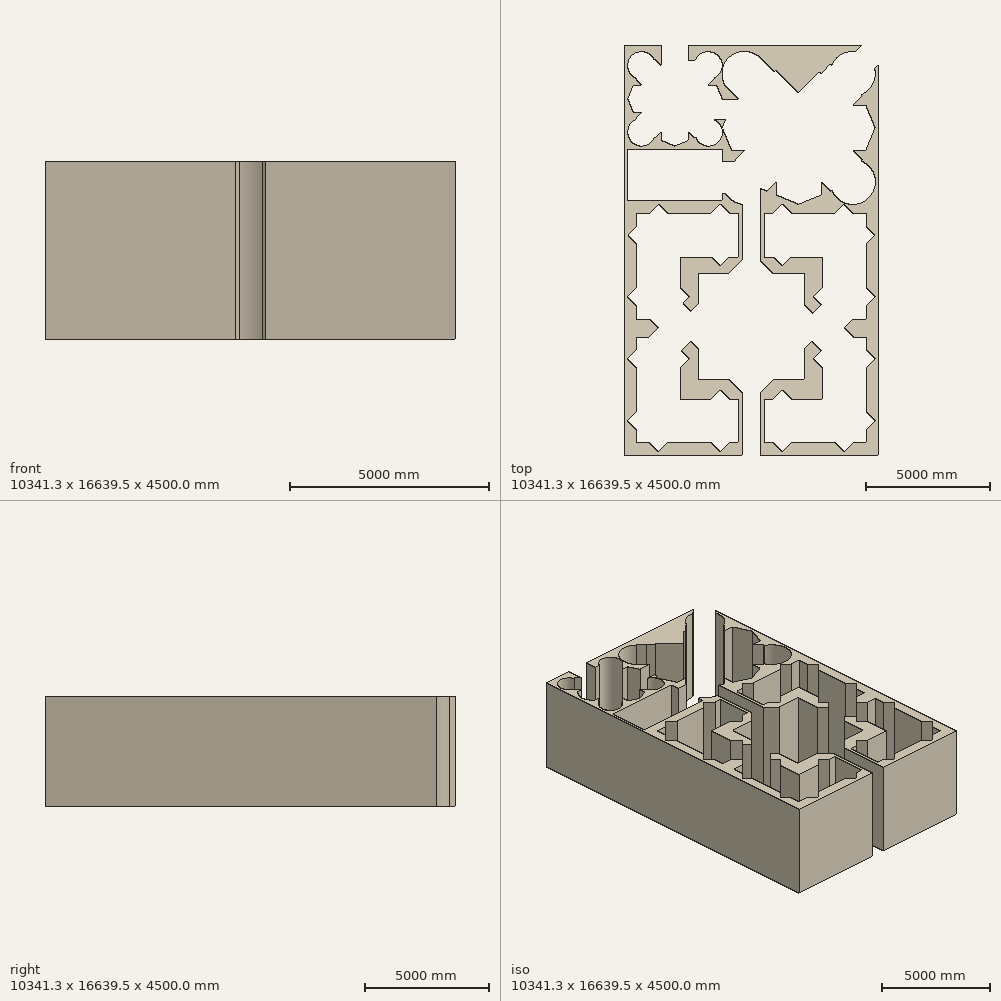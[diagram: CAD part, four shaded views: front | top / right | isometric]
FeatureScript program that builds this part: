
annotation { "Feature Type Name" : "Feature", "Feature Type Description" : "" }
export const myFeature = defineFeature(function(context is Context, id is Id, definition is map)
    precondition{}
    {
        {
            var Q0;
            Q0=qCreatedBy(makeId("Top.planeOp"),FACE);
            var sketch = newSketch(context, id + "F0", { "sketchPlane" : qUnion([Q0])});
            skLineSegment(sketch, "E0", {"start": v(6052.83, 6645.12) * mm, "end": v(5685.2, 6277.49) * mm});
            skLineSegment(sketch, "E1", {"start": v(6052.83, 5389.96) * mm, "end": v(6572.74, 5389.96) * mm});
            skLineSegment(sketch, "E2", {"start": v(6052.83, 9155.44) * mm, "end": v(5685.2, 8787.81) * mm});
            skLineSegment(sketch, "E3", {"start": v(6052.83, 10410.6) * mm, "end": v(6572.74, 10410.6) * mm});
            skLineSegment(sketch, "E4", {"start": v(5685.2, 13808.46) * mm, "end": v(6052.83, 13440.84) * mm});
            skLineSegment(sketch, "E5", {"start": v(6052.83, 14176.1) * mm, "end": v(5685.2, 13808.46) * mm});
            skLineSegment(sketch, "E6", {"start": v(8563.16, 12920.93) * mm, "end": v(9083.06, 12920.93) * mm});
            skLineSegment(sketch, "E7", {"start": v(9818.32, 12920.93) * mm, "end": v(10188.23, 12920.93) * mm});
            skLineSegment(sketch, "E8", {"start": v(10188.23, 12920.93) * mm, "end": v(10188.23, 14696) * mm});
            skLineSegment(sketch, "E9", {"start": v(10188.23, 14696) * mm, "end": v(9818.32, 14696) * mm});
            skLineSegment(sketch, "E10", {"start": v(9818.32, 5389.96) * mm, "end": v(10188.23, 5389.96) * mm});
            skLineSegment(sketch, "E11", {"start": v(10188.23, 7165.02) * mm, "end": v(9818.32, 7165.02) * mm});
            skLineSegment(sketch, "E12", {"start": v(11223.48, 5389.96) * mm, "end": v(11593.39, 5389.96) * mm});
            skLineSegment(sketch, "E13", {"start": v(13583.8, 7165.02) * mm, "end": v(12328.65, 7165.02) * mm});
            skLineSegment(sketch, "E14", {"start": v(11593.39, 7165.02) * mm, "end": v(11223.48, 7165.02) * mm});
            skLineSegment(sketch, "E15", {"start": v(13540.37, 9112) * mm, "end": v(13216.18, 8787.81) * mm});
            skLineSegment(sketch, "E16", {"start": v(13216.18, 11298.14) * mm, "end": v(13540.37, 10973.95) * mm});
            skLineSegment(sketch, "E17", {"start": v(13583.8, 11665.77) * mm, "end": v(13216.18, 11298.14) * mm});
            skLineSegment(sketch, "E18", {"start": v(13583.8, 12920.93) * mm, "end": v(13583.8, 11665.77) * mm});
            skLineSegment(sketch, "E19", {"start": v(11223.48, 12920.93) * mm, "end": v(11593.39, 12920.93) * mm});
            skLineSegment(sketch, "E20", {"start": v(12328.65, 12920.93) * mm, "end": v(13583.8, 12920.93) * mm});
            skLineSegment(sketch, "E21", {"start": v(10055.24, 16875.43) * mm, "end": v(10077.3, 16821.95) * mm});
            skLineSegment(sketch, "E22", {"start": v(13609.52, 20438.13) * mm, "end": v(13903.7, 20733.02) * mm});
            skLineSegment(sketch, "E23", {"start": v(6015.44, 18546.52) * mm, "end": v(6032.8, 18504.43) * mm});
            skLineSegment(sketch, "E24", {"start": v(7827.9, 11665.77) * mm, "end": v(7827.9, 12920.93) * mm});
            skLineSegment(sketch, "E25", {"start": v(10188.23, 5389.96) * mm, "end": v(10188.23, 7165.02) * mm});
            skLineSegment(sketch, "E26", {"start": v(8563.16, 12920.93) * mm, "end": v(7827.9, 12920.93) * mm});
            skLineSegment(sketch, "E27", {"start": v(8257.01, 9497.68) * mm, "end": v(8543.44, 9211.25) * mm});
            skLineSegment(sketch, "E28", {"start": v(13148.68, 9503.7) * mm, "end": v(13540.37, 9112) * mm});
            skLineSegment(sketch, "E29", {"start": v(13816.94, 10036.96) * mm, "end": v(14141.14, 9712.77) * mm});
            skLineSegment(sketch, "E30", {"start": v(13210.16, 10643.74) * mm, "end": v(13540.37, 10973.95) * mm});
            skLineSegment(sketch, "E31", {"start": v(13528.56, 20356.5) * mm, "end": v(13903.7, 20733.02) * mm});
            skLineSegment(sketch, "E32", {"start": v(10077.3, 16821.95) * mm, "end": v(9520.98, 16821.95) * mm});
            skLineSegment(sketch, "E33", {"start": v(9654.14, 15488.62) * mm, "end": v(9520.98, 15488.62) * mm});
            skLineSegment(sketch, "E34", {"start": v(9520.98, 15204.7) * mm, "end": v(5685.2, 15204.7) * mm});
            skLineSegment(sketch, "E35", {"start": v(14917.97, 21263) * mm, "end": v(15200.59, 21511.85) * mm});
            skLineSegment(sketch, "E36", {"start": v(9176.96, 18507.2) * mm, "end": v(9520.98, 18507.2) * mm});
            skArc(sketch, "E37", {"start": v(15166.58, 19511.46) * mm, "mid": v(15633.58, 19946.01) * mm, "end": v(15702.28, 20580.2) * mm});
            skArc(sketch, "E38", {"start": v(13978.32, 15621.76) * mm, "mid": v(15468.53, 15323.83) * mm, "end": v(15170.85, 16814.1) * mm});
            skArc(sketch, "E39", {"start": v(6032.8, 18504.43) * mm, "mid": v(5851.1, 17589.86) * mm, "end": v(6764.95, 17775.2) * mm});
            skArc(sketch, "E40", {"start": v(8451.28, 17776.09) * mm, "mid": v(9367.75, 17592.12) * mm, "end": v(9176.96, 18507.2) * mm});
            skArc(sketch, "E41", {"start": v(6762.28, 20910.78) * mm, "mid": v(5847.8, 21093.33) * mm, "end": v(6032.5, 20179.29) * mm});
            skLineSegment(sketch, "E42", {"start": v(9806.63, 12260.86) * mm, "end": v(10338.23, 12792.45) * mm});
            skLineSegment(sketch, "E43", {"start": v(11073.48, 12780.42) * mm, "end": v(11593.05, 12260.86) * mm});
            skLineSegment(sketch, "E44", {"start": v(7038.77, 21511.85) * mm, "end": v(8162.46, 21511.85) * mm});
            skLineSegment(sketch, "E45", {"start": v(10338.23, 4872.33) * mm, "end": v(11073.48, 4872.33) * mm});
            skLineSegment(sketch, "E46", {"start": v(15170.85, 16814.1) * mm, "end": v(15194.5, 16873.27) * mm});
            skLineSegment(sketch, "E47", {"start": v(5685.2, 6277.49) * mm, "end": v(6052.83, 5909.86) * mm});
            skLineSegment(sketch, "E48", {"start": v(6052.83, 5909.86) * mm, "end": v(6052.83, 5389.96) * mm});
            skLineSegment(sketch, "E49", {"start": v(7264.56, 9718.79) * mm, "end": v(6940.37, 10042.98) * mm});
            skLineSegment(sketch, "E50", {"start": v(6940.37, 10042.98) * mm, "end": v(6572.74, 9675.35) * mm});
            skLineSegment(sketch, "E51", {"start": v(6572.74, 9675.35) * mm, "end": v(6052.83, 9675.35) * mm});
            skLineSegment(sketch, "E52", {"start": v(6052.83, 9675.35) * mm, "end": v(6052.83, 9155.44) * mm});
            skLineSegment(sketch, "E53", {"start": v(5685.2, 8787.81) * mm, "end": v(6052.83, 8420.19) * mm});
            skLineSegment(sketch, "E54", {"start": v(6052.83, 8420.19) * mm, "end": v(6052.83, 7900.28) * mm});
            skLineSegment(sketch, "E55", {"start": v(6052.83, 7900.28) * mm, "end": v(6052.83, 6645.12) * mm});
            skLineSegment(sketch, "E56", {"start": v(6572.74, 14696) * mm, "end": v(6052.83, 14696) * mm});
            skLineSegment(sketch, "E57", {"start": v(6052.83, 14696) * mm, "end": v(6052.83, 14176.1) * mm});
            skLineSegment(sketch, "E58", {"start": v(9083.06, 12920.93) * mm, "end": v(9450.7, 12553.3) * mm});
            skLineSegment(sketch, "E59", {"start": v(9450.7, 12553.3) * mm, "end": v(9818.32, 12920.93) * mm});
            skLineSegment(sketch, "E60", {"start": v(9818.32, 14696) * mm, "end": v(9450.7, 15063.63) * mm});
            skLineSegment(sketch, "E61", {"start": v(9450.7, 15063.63) * mm, "end": v(9083.06, 14696) * mm});
            skLineSegment(sketch, "E62", {"start": v(9083.06, 14696) * mm, "end": v(7308, 14696) * mm});
            skLineSegment(sketch, "E63", {"start": v(7308, 14696) * mm, "end": v(6940.37, 15063.63) * mm});
            skLineSegment(sketch, "E64", {"start": v(6940.37, 15063.63) * mm, "end": v(6572.74, 14696) * mm});
            skLineSegment(sketch, "E65", {"start": v(9083.06, 5389.96) * mm, "end": v(9450.7, 5022.33) * mm});
            skLineSegment(sketch, "E66", {"start": v(9450.7, 5022.33) * mm, "end": v(9818.32, 5389.96) * mm});
            skLineSegment(sketch, "E67", {"start": v(9818.32, 7165.02) * mm, "end": v(9450.7, 7532.65) * mm});
            skLineSegment(sketch, "E68", {"start": v(9450.7, 7532.65) * mm, "end": v(9083.06, 7165.02) * mm});
            skLineSegment(sketch, "E69", {"start": v(6572.74, 5389.96) * mm, "end": v(6940.37, 5022.33) * mm});
            skLineSegment(sketch, "E70", {"start": v(6940.37, 5022.33) * mm, "end": v(7308, 5389.96) * mm});
            skLineSegment(sketch, "E71", {"start": v(7308, 5389.96) * mm, "end": v(9083.06, 5389.96) * mm});
            skLineSegment(sketch, "E72", {"start": v(9083.06, 7165.02) * mm, "end": v(7827.9, 7165.02) * mm});
            skLineSegment(sketch, "E73", {"start": v(7827.9, 7165.02) * mm, "end": v(7827.9, 7900.28) * mm});
            skLineSegment(sketch, "E74", {"start": v(7827.9, 7900.28) * mm, "end": v(7827.9, 8420.19) * mm});
            skLineSegment(sketch, "E75", {"start": v(7827.9, 8420.19) * mm, "end": v(8195.53, 8787.81) * mm});
            skLineSegment(sketch, "E76", {"start": v(8195.53, 8787.81) * mm, "end": v(7871.34, 9112) * mm});
            skLineSegment(sketch, "E77", {"start": v(11593.39, 5389.96) * mm, "end": v(11961.02, 5022.33) * mm});
            skLineSegment(sketch, "E78", {"start": v(11961.02, 5022.33) * mm, "end": v(12328.65, 5389.96) * mm});
            skLineSegment(sketch, "E79", {"start": v(12328.65, 7165.02) * mm, "end": v(11961.02, 7532.65) * mm});
            skLineSegment(sketch, "E80", {"start": v(11961.02, 7532.65) * mm, "end": v(11593.39, 7165.02) * mm});
            skLineSegment(sketch, "E81", {"start": v(14103.71, 5389.96) * mm, "end": v(14471.34, 5022.33) * mm});
            skLineSegment(sketch, "E82", {"start": v(14471.34, 5022.33) * mm, "end": v(14838.97, 5389.96) * mm});
            skLineSegment(sketch, "E83", {"start": v(12328.65, 5389.96) * mm, "end": v(13583.8, 5389.96) * mm});
            skLineSegment(sketch, "E84", {"start": v(13583.8, 5389.96) * mm, "end": v(14103.71, 5389.96) * mm});
            skLineSegment(sketch, "E85", {"start": v(14838.97, 5389.96) * mm, "end": v(15358.88, 5389.96) * mm});
            skLineSegment(sketch, "E86", {"start": v(15358.88, 5389.96) * mm, "end": v(15358.88, 5909.86) * mm});
            skLineSegment(sketch, "E87", {"start": v(15358.88, 5909.86) * mm, "end": v(15726.5, 6277.49) * mm});
            skLineSegment(sketch, "E88", {"start": v(15726.5, 6277.49) * mm, "end": v(15358.88, 6645.12) * mm});
            skLineSegment(sketch, "E89", {"start": v(15358.88, 8420.19) * mm, "end": v(15726.5, 8787.81) * mm});
            skLineSegment(sketch, "E90", {"start": v(15726.5, 8787.81) * mm, "end": v(15358.88, 9155.44) * mm});
            skLineSegment(sketch, "E91", {"start": v(14838.97, 9675.35) * mm, "end": v(14471.34, 10042.98) * mm});
            skLineSegment(sketch, "E92", {"start": v(14471.34, 10042.98) * mm, "end": v(14141.14, 9712.77) * mm});
            skLineSegment(sketch, "E93", {"start": v(15358.88, 6645.12) * mm, "end": v(15358.88, 7900.28) * mm});
            skLineSegment(sketch, "E94", {"start": v(15358.88, 7900.28) * mm, "end": v(15358.88, 8420.19) * mm});
            skLineSegment(sketch, "E95", {"start": v(15358.88, 9155.44) * mm, "end": v(15358.88, 9675.35) * mm});
            skLineSegment(sketch, "E96", {"start": v(15358.88, 9675.35) * mm, "end": v(14838.97, 9675.35) * mm});
            skLineSegment(sketch, "E97", {"start": v(13216.18, 8787.81) * mm, "end": v(13583.8, 8420.19) * mm});
            skLineSegment(sketch, "E98", {"start": v(13583.8, 8420.19) * mm, "end": v(13583.8, 7165.02) * mm});
            skLineSegment(sketch, "E99", {"start": v(14838.97, 10410.6) * mm, "end": v(15358.88, 10410.6) * mm});
            skLineSegment(sketch, "E100", {"start": v(15358.88, 10410.6) * mm, "end": v(15358.88, 10930.51) * mm});
            skLineSegment(sketch, "E101", {"start": v(15358.88, 10930.51) * mm, "end": v(15726.5, 11298.14) * mm});
            skLineSegment(sketch, "E102", {"start": v(15726.5, 11298.14) * mm, "end": v(15358.88, 11665.77) * mm});
            skLineSegment(sketch, "E103", {"start": v(14838.97, 14696) * mm, "end": v(14471.34, 15063.63) * mm});
            skLineSegment(sketch, "E104", {"start": v(14471.34, 15063.63) * mm, "end": v(14103.71, 14696) * mm});
            skLineSegment(sketch, "E105", {"start": v(15358.88, 11665.77) * mm, "end": v(15358.88, 12920.93) * mm});
            skLineSegment(sketch, "E106", {"start": v(15358.88, 12920.93) * mm, "end": v(15358.88, 13440.84) * mm});
            skLineSegment(sketch, "E107", {"start": v(15358.88, 13440.84) * mm, "end": v(15726.5, 13808.46) * mm});
            skLineSegment(sketch, "E108", {"start": v(15726.5, 13808.46) * mm, "end": v(15358.88, 14176.1) * mm});
            skLineSegment(sketch, "E109", {"start": v(15358.88, 14176.1) * mm, "end": v(15358.88, 14696) * mm});
            skLineSegment(sketch, "E110", {"start": v(15358.88, 14696) * mm, "end": v(14838.97, 14696) * mm});
            skLineSegment(sketch, "E111", {"start": v(11593.39, 12920.93) * mm, "end": v(11961.02, 12553.3) * mm});
            skLineSegment(sketch, "E112", {"start": v(11961.02, 12553.3) * mm, "end": v(12328.65, 12920.93) * mm});
            skLineSegment(sketch, "E113", {"start": v(12328.65, 14696) * mm, "end": v(11961.02, 15063.63) * mm});
            skLineSegment(sketch, "E114", {"start": v(11961.02, 15063.63) * mm, "end": v(11593.39, 14696) * mm});
            skLineSegment(sketch, "E115", {"start": v(14103.71, 14696) * mm, "end": v(13583.8, 14696) * mm});
            skLineSegment(sketch, "E116", {"start": v(13583.8, 14696) * mm, "end": v(12328.65, 14696) * mm});
            skLineSegment(sketch, "E117", {"start": v(11593.39, 14696) * mm, "end": v(11223.48, 14696) * mm});
            skLineSegment(sketch, "E118", {"start": v(11223.48, 14696) * mm, "end": v(11223.48, 12920.93) * mm});
            skLineSegment(sketch, "E119", {"start": v(10055.24, 16875.43) * mm, "end": v(10433.14, 17254.22) * mm});
            skLineSegment(sketch, "E120", {"start": v(10433.14, 17254.22) * mm, "end": v(9898.48, 17254.22) * mm});
            skLineSegment(sketch, "E121", {"start": v(9898.48, 17254.22) * mm, "end": v(9520.97, 18166.39) * mm});
            skLineSegment(sketch, "E122", {"start": v(15352.05, 17254.22) * mm, "end": v(14819.13, 17254.22) * mm});
            skLineSegment(sketch, "E123", {"start": v(14819.13, 17254.22) * mm, "end": v(15194.5, 16873.27) * mm});
            skLineSegment(sketch, "E124", {"start": v(6572.74, 10410.6) * mm, "end": v(6940.37, 10042.98) * mm});
            skLineSegment(sketch, "E125", {"start": v(6940.37, 10042.98) * mm, "end": v(7264.9, 10367.52) * mm});
            skLineSegment(sketch, "E126", {"start": v(12856.24, 10997.67) * mm, "end": v(12856.24, 12260.86) * mm});
            skLineSegment(sketch, "E127", {"start": v(12856.24, 12260.86) * mm, "end": v(11593.05, 12260.86) * mm});
            skLineSegment(sketch, "E128", {"start": v(9806.63, 7948.06) * mm, "end": v(8543.44, 7948.06) * mm});
            skLineSegment(sketch, "E129", {"start": v(8543.44, 7948.06) * mm, "end": v(8543.44, 9211.25) * mm});
            skLineSegment(sketch, "E130", {"start": v(7589.1, 10043.32) * mm, "end": v(7264.56, 9718.79) * mm});
            skLineSegment(sketch, "E131", {"start": v(7264.56, 9718.79) * mm, "end": v(7589.1, 10043.32) * mm});
            skLineSegment(sketch, "E132", {"start": v(7589.1, 10043.32) * mm, "end": v(7264.9, 10367.52) * mm});
            skLineSegment(sketch, "E133", {"start": v(13816.94, 10036.96) * mm, "end": v(14147.15, 10367.17) * mm});
            skLineSegment(sketch, "E134", {"start": v(14147.15, 10367.17) * mm, "end": v(14471.34, 10042.98) * mm});
            skLineSegment(sketch, "E135", {"start": v(14471.34, 10042.98) * mm, "end": v(14838.97, 10410.6) * mm});
            skLineSegment(sketch, "E136", {"start": v(12623.74, 15063.63) * mm, "end": v(13530.42, 15437.21) * mm});
            skLineSegment(sketch, "E137", {"start": v(13530.42, 15437.21) * mm, "end": v(13530.25, 15979.46) * mm});
            skLineSegment(sketch, "E138", {"start": v(13530.25, 15979.46) * mm, "end": v(13914.31, 15595.4) * mm});
            skLineSegment(sketch, "E139", {"start": v(13914.31, 15595.4) * mm, "end": v(13978.32, 15621.76) * mm});
            skLineSegment(sketch, "E140", {"start": v(14814.35, 17254.22) * mm, "end": v(15349, 17254.22) * mm});
            skLineSegment(sketch, "E141", {"start": v(15349, 17254.22) * mm, "end": v(15726.51, 18166.39) * mm});
            skLineSegment(sketch, "E142", {"start": v(15726.51, 18166.39) * mm, "end": v(15347.51, 19076.56) * mm});
            skLineSegment(sketch, "E143", {"start": v(15347.51, 19076.56) * mm, "end": v(14814.34, 19076.56) * mm});
            skLineSegment(sketch, "E144", {"start": v(9520.98, 18507.2) * mm, "end": v(9662.89, 18507.2) * mm});
            skLineSegment(sketch, "E145", {"start": v(9662.89, 18507.2) * mm, "end": v(9520.97, 18166.39) * mm});
            skLineSegment(sketch, "E146", {"start": v(9173.17, 20180.05) * mm, "end": v(9190.44, 20138.35) * mm});
            skLineSegment(sketch, "E147", {"start": v(9190.44, 20138.35) * mm, "end": v(8954.2, 19901.55) * mm});
            skLineSegment(sketch, "E148", {"start": v(8954.2, 19901.55) * mm, "end": v(9286.23, 19907.1) * mm});
            skLineSegment(sketch, "E149", {"start": v(9286.23, 19907.1) * mm, "end": v(9520.98, 19340.31) * mm});
            skLineSegment(sketch, "E150", {"start": v(9520.98, 19340.31) * mm, "end": v(10169.4, 19340.31) * mm});
            skLineSegment(sketch, "E151", {"start": v(10169.4, 19340.31) * mm, "end": v(9676.55, 19833.16) * mm});
            skLineSegment(sketch, "E152", {"start": v(11073.48, 12780.42) * mm, "end": v(11073.48, 15054.7) * mm});
            skLineSegment(sketch, "E153", {"start": v(11073.48, 15054.7) * mm, "end": v(11073.48, 15333.96) * mm});
            skLineSegment(sketch, "E154", {"start": v(11073.48, 15333.96) * mm, "end": v(11073.48, 15706.8) * mm});
            skLineSegment(sketch, "E155", {"start": v(11073.48, 15706.8) * mm, "end": v(11268.91, 15627.11) * mm});
            skLineSegment(sketch, "E156", {"start": v(11268.91, 15627.11) * mm, "end": v(11345.9, 15595.72) * mm});
            skLineSegment(sketch, "E157", {"start": v(11345.9, 15595.72) * mm, "end": v(11718.06, 15968.75) * mm});
            skLineSegment(sketch, "E158", {"start": v(11718.06, 15968.75) * mm, "end": v(11718.06, 15440.75) * mm});
            skLineSegment(sketch, "E159", {"start": v(11718.06, 15440.75) * mm, "end": v(12623.74, 15063.63) * mm});
            skLineSegment(sketch, "E160", {"start": v(15166.58, 19511.46) * mm, "end": v(15191.76, 19450.69) * mm});
            skLineSegment(sketch, "E161", {"start": v(15191.76, 19450.69) * mm, "end": v(14818.51, 19076.56) * mm});
            skLineSegment(sketch, "E162", {"start": v(14818.51, 19076.56) * mm, "end": v(15346.72, 19076.56) * mm});
            skLineSegment(sketch, "E163", {"start": v(13903.7, 20733.02) * mm, "end": v(13973.1, 20704.32) * mm});
            skArc(sketch, "E164", {"start": v(14917.97, 21263) * mm, "mid": v(14352.24, 21141.45) * mm, "end": v(13973.1, 20704.32) * mm});
            skLineSegment(sketch, "E165", {"start": v(11337.15, 20730.62) * mm, "end": v(11633.78, 20433.98) * mm});
            skLineSegment(sketch, "E166", {"start": v(11633.78, 20433.98) * mm, "end": v(11704.5, 20504.7) * mm});
            skLineSegment(sketch, "E167", {"start": v(11704.5, 20504.7) * mm, "end": v(12621.46, 19587.73) * mm});
            skLineSegment(sketch, "E168", {"start": v(12621.46, 19587.73) * mm, "end": v(13457.72, 20427.08) * mm});
            skLineSegment(sketch, "E169", {"start": v(13457.72, 20427.08) * mm, "end": v(13528.56, 20356.5) * mm});
            skLineSegment(sketch, "E170", {"start": v(9520.98, 16821.95) * mm, "end": v(9520.98, 17276.6) * mm});
            skLineSegment(sketch, "E171", {"start": v(9520.98, 17276.6) * mm, "end": v(5685.2, 17276.6) * mm});
            skLineSegment(sketch, "E172", {"start": v(5685.2, 17276.6) * mm, "end": v(5685.2, 15204.7) * mm});
            skLineSegment(sketch, "E173", {"start": v(5685.2, 15204.7) * mm, "end": v(9520.98, 15204.7) * mm});
            skLineSegment(sketch, "E174", {"start": v(9520.98, 15204.7) * mm, "end": v(9520.98, 15488.62) * mm});
            skLineSegment(sketch, "E175", {"start": v(9520.98, 15488.62) * mm, "end": v(9654.14, 15488.62) * mm});
            skArc(sketch, "E176", {"start": v(9654.14, 15488.62) * mm, "mid": v(9950.39, 15203.99) * mm, "end": v(10338.23, 15068.48) * mm});
            skLineSegment(sketch, "E177", {"start": v(10338.23, 15068.48) * mm, "end": v(10338.23, 15054.7) * mm});
            skLineSegment(sketch, "E178", {"start": v(10338.23, 15054.7) * mm, "end": v(10338.23, 12792.45) * mm});
            skLineSegment(sketch, "E179", {"start": v(5685.2, 19344.5) * mm, "end": v(5685.2, 19344.48) * mm});
            skLineSegment(sketch, "E180", {"start": v(6761.6, 20912.4) * mm, "end": v(6801.04, 20928.75) * mm});
            skLineSegment(sketch, "E181", {"start": v(6801.04, 20928.75) * mm, "end": v(7034.99, 20697.35) * mm});
            skLineSegment(sketch, "E182", {"start": v(7034.99, 20697.35) * mm, "end": v(7038.77, 21511.85) * mm});
            skLineSegment(sketch, "E183", {"start": v(7038.77, 21511.85) * mm, "end": v(5535.2, 21511.85) * mm});
            skLineSegment(sketch, "E184", {"start": v(5535.2, 21511.85) * mm, "end": v(5535.2, 19907.1) * mm});
            skLineSegment(sketch, "E185", {"start": v(15876.5, 20733.62) * mm, "end": v(15876.5, 21511.85) * mm});
            skLineSegment(sketch, "E186", {"start": v(15876.5, 21511.85) * mm, "end": v(15200.59, 21511.85) * mm});
            skLineSegment(sketch, "E187", {"start": v(15200.59, 21511.85) * mm, "end": v(8162.46, 21511.85) * mm});
            skLineSegment(sketch, "E188", {"start": v(8162.46, 21511.85) * mm, "end": v(8162.46, 21269.15) * mm});
            skLineSegment(sketch, "E189", {"start": v(8162.46, 21269.15) * mm, "end": v(8162.46, 20917.14) * mm});
            skLineSegment(sketch, "E190", {"start": v(8162.46, 20917.14) * mm, "end": v(8441.3, 20911.54) * mm});
            skArc(sketch, "E191", {"start": v(9173.17, 20180.05) * mm, "mid": v(9354.77, 21093.62) * mm, "end": v(8441.3, 20911.54) * mm});
            skLineSegment(sketch, "E192", {"start": v(15876.5, 17254.22) * mm, "end": v(15876.5, 19076.56) * mm});
            skLineSegment(sketch, "E193", {"start": v(15876.5, 19076.56) * mm, "end": v(15876.5, 20733.62) * mm});
            skLineSegment(sketch, "E194", {"start": v(15876.5, 20733.62) * mm, "end": v(15702.28, 20580.2) * mm});
            skLineSegment(sketch, "E195", {"start": v(5535.2, 19907.1) * mm, "end": v(5535.2, 18780.66) * mm});
            skLineSegment(sketch, "E196", {"start": v(5535.2, 18780.66) * mm, "end": v(5535.2, 4872.33) * mm});
            skLineSegment(sketch, "E197", {"start": v(5535.2, 4872.33) * mm, "end": v(10338.23, 4872.33) * mm});
            skLineSegment(sketch, "E198", {"start": v(10338.23, 4872.33) * mm, "end": v(10338.23, 6645.12) * mm});
            skLineSegment(sketch, "E199", {"start": v(10338.23, 6645.12) * mm, "end": v(10338.23, 7416.47) * mm});
            skLineSegment(sketch, "E200", {"start": v(10338.23, 7416.47) * mm, "end": v(9806.63, 7948.06) * mm});
            skArc(sketch, "E201", {"start": v(11010.74, 21057.03) * mm, "mid": v(9808.13, 21028.87) * mm, "end": v(9676.55, 19833.16) * mm});
            skLineSegment(sketch, "E202", {"start": v(11010.74, 21057.03) * mm, "end": v(11337.15, 20730.62) * mm});
            skLineSegment(sketch, "E203", {"start": v(12856.24, 9211.25) * mm, "end": v(12856.24, 7948.06) * mm});
            skLineSegment(sketch, "E204", {"start": v(12856.24, 7948.06) * mm, "end": v(11593.05, 7948.06) * mm});
            skLineSegment(sketch, "E205", {"start": v(11593.05, 7948.06) * mm, "end": v(11073.48, 7428.5) * mm});
            skLineSegment(sketch, "E206", {"start": v(11073.48, 7428.5) * mm, "end": v(11073.48, 6645.12) * mm});
            skLineSegment(sketch, "E207", {"start": v(11073.48, 6645.12) * mm, "end": v(11073.48, 4872.33) * mm});
            skLineSegment(sketch, "E208", {"start": v(11073.48, 4872.33) * mm, "end": v(15876.5, 4872.33) * mm});
            skLineSegment(sketch, "E209", {"start": v(15876.5, 4872.33) * mm, "end": v(15876.5, 17254.22) * mm});
            skLineSegment(sketch, "E210", {"start": v(8246.74, 10700.96) * mm, "end": v(8543.44, 10997.67) * mm});
            skLineSegment(sketch, "E211", {"start": v(8543.44, 9211.25) * mm, "end": v(8257.01, 9497.68) * mm});
            skLineSegment(sketch, "E212", {"start": v(8257.01, 9497.68) * mm, "end": v(7871.34, 9112) * mm});
            skLineSegment(sketch, "E213", {"start": v(7871.34, 9112) * mm, "end": v(8257.01, 9497.68) * mm});
            skLineSegment(sketch, "E214", {"start": v(13210.16, 10643.74) * mm, "end": v(12856.24, 10997.67) * mm});
            skLineSegment(sketch, "E215", {"start": v(12856.24, 9211.25) * mm, "end": v(13148.68, 9503.7) * mm});
            skLineSegment(sketch, "E216", {"start": v(8543.44, 10997.67) * mm, "end": v(8543.44, 12260.86) * mm});
            skLineSegment(sketch, "E217", {"start": v(8543.44, 12260.86) * mm, "end": v(9806.63, 12260.86) * mm});
            skLineSegment(sketch, "E218", {"start": v(6052.83, 13440.84) * mm, "end": v(6052.83, 11665.77) * mm});
            skLineSegment(sketch, "E219", {"start": v(6052.83, 11665.77) * mm, "end": v(5685.2, 11298.14) * mm});
            skLineSegment(sketch, "E220", {"start": v(5685.2, 11298.14) * mm, "end": v(6052.83, 10930.51) * mm});
            skLineSegment(sketch, "E221", {"start": v(6052.83, 10930.51) * mm, "end": v(6052.83, 10410.6) * mm});
            skLineSegment(sketch, "E222", {"start": v(8246.74, 10700.96) * mm, "end": v(7922.55, 11025.16) * mm});
            skLineSegment(sketch, "E223", {"start": v(7922.55, 11025.16) * mm, "end": v(8195.53, 11298.14) * mm});
            skLineSegment(sketch, "E224", {"start": v(8195.53, 11298.14) * mm, "end": v(7827.9, 11665.77) * mm});
            skLineSegment(sketch, "E225", {"start": v(6764.95, 17775.2) * mm, "end": v(6813.23, 17755.5) * mm});
            skLineSegment(sketch, "E226", {"start": v(6813.23, 17755.5) * mm, "end": v(7043.27, 17986.08) * mm});
            skLineSegment(sketch, "E227", {"start": v(7043.27, 17986.08) * mm, "end": v(7043.27, 17659.72) * mm});
            skLineSegment(sketch, "E228", {"start": v(7043.27, 17659.72) * mm, "end": v(7603.1, 17426.6) * mm});
            skLineSegment(sketch, "E229", {"start": v(7603.1, 17426.6) * mm, "end": v(8163.53, 17657.53) * mm});
            skLineSegment(sketch, "E230", {"start": v(8163.53, 17657.53) * mm, "end": v(8163.42, 17992.7) * mm});
            skLineSegment(sketch, "E231", {"start": v(8163.42, 17992.7) * mm, "end": v(8400.82, 17755.3) * mm});
            skLineSegment(sketch, "E232", {"start": v(8400.82, 17755.3) * mm, "end": v(8451.28, 17776.09) * mm});
            skLineSegment(sketch, "E233", {"start": v(6015.44, 18546.52) * mm, "end": v(6249.03, 18780.66) * mm});
            skLineSegment(sketch, "E234", {"start": v(6249.03, 18780.66) * mm, "end": v(5918.55, 18780.66) * mm});
            skLineSegment(sketch, "E235", {"start": v(5918.55, 18780.66) * mm, "end": v(5685.2, 19344.5) * mm});
            skLineSegment(sketch, "E236", {"start": v(5685.2, 19344.5) * mm, "end": v(5919.47, 19907.1) * mm});
            skLineSegment(sketch, "E237", {"start": v(5919.47, 19907.1) * mm, "end": v(6249.03, 19907.1) * mm});
            skLineSegment(sketch, "E238", {"start": v(6249.03, 19907.1) * mm, "end": v(6016.36, 20139.77) * mm});
            skLineSegment(sketch, "E239", {"start": v(6016.36, 20139.77) * mm, "end": v(6032.5, 20179.29) * mm});
            skLineSegment(sketch, "E240", {"start": v(11223.48, 5389.96) * mm, "end": v(11223.48, 7165.02) * mm});
            skSolve(sketch);
        }
        {
            var Q0;
            Q0=makeQuery(id+"F0.imprint","IMPRINT",FACE,{"disambiguationData":[TD([[makeQuery(id+"F0.imprint","IMPRINT",EDGE,{"derivedFrom":sQuery(id+"F0.wireOp",EDGE,"E12")}),-1.0]])]});
            var Q1;
            Q1=makeQuery(id+"F0.imprint","IMPRINT",FACE,{"disambiguationData":[TD([[makeQuery(id+"F0.imprint","IMPRINT",EDGE,{"derivedFrom":sQuery(id+"F0.wireOp",EDGE,"E0")}),-1.0]])]});
            var Q2;
            Q2=makeQuery(id+"F0.imprint","IMPRINT",FACE,{"disambiguationData":[TD([[makeQuery(id+"F0.imprint","IMPRINT",EDGE,{"derivedFrom":sQuery(id+"F0.wireOp",EDGE,"E31")}),1.0]])]});
            extrude(context, id + "F1", {"entities" : qUnion([Q0, Q1, Q2]), "depth" : 4500 * mm, "offsetDistance" : 25.4 * mm});
        }
    });
